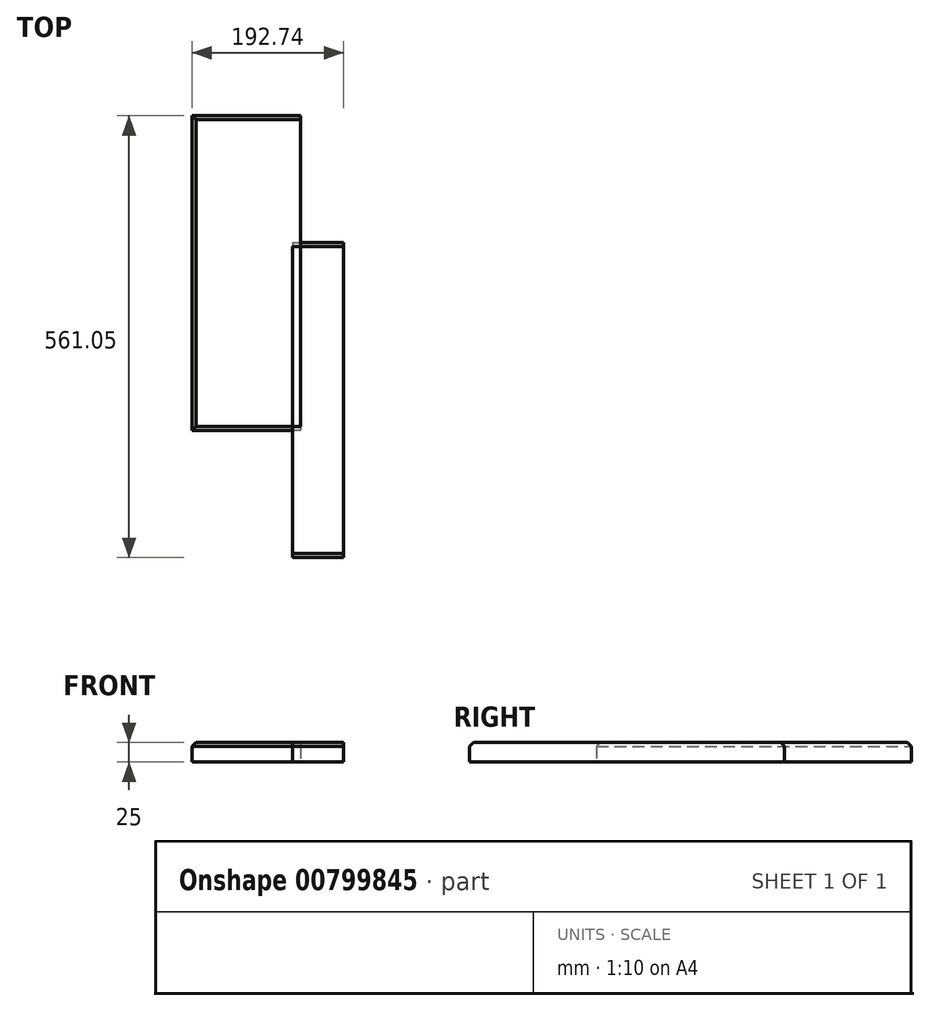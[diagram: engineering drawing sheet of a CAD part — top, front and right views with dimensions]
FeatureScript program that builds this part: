
annotation { "Feature Type Name" : "Feature", "Feature Type Description" : "" }
export const myFeature = defineFeature(function(context is Context, id is Id, definition is map)
    precondition{}
    {
        {
            var Q0;
            Q0=qCreatedBy(makeId("Top.planeOp"),FACE);
            var sketch = newSketch(context, id + "F0", { "sketchPlane" : qUnion([Q0])});
            skLineSegment(sketch, "E0", {"start": v(-106.87, 169.05) * mm, "end": v(106.6, -169.22) * mm});
            skLineSegment(sketch, "E1", {"start": v(106.6, -169.22) * mm, "end": v(-106.87, 169.05) * mm});
            skArc(sketch, "E2", {"start": v(106.6, -169.22) * mm, "mid": v(169.14, 106.74) * mm, "end": v(-106.87, 169.05) * mm});
            skSolve(sketch);
        }
        {
            var Q0;
            Q0=qCreatedBy(makeId("Top.planeOp"),FACE);
            var sketch = newSketch(context, id + "F1", { "sketchPlane" : qUnion([Q0])});
            skLineSegment(sketch, "E3.bottom", {"start": v(-271.16, 238.95) * mm, "end": v(-206.16, 238.95) * mm});
            skLineSegment(sketch, "E3.top", {"start": v(-271.16, -161.05) * mm, "end": v(-206.16, -161.05) * mm});
            skLineSegment(sketch, "E3.left", {"start": v(-271.16, 238.95) * mm, "end": v(-271.16, -161.05) * mm});
            skLineSegment(sketch, "E3.right", {"start": v(-206.16, 238.95) * mm, "end": v(-206.16, -161.05) * mm});
            skSolve(sketch);
        }
        {
            var Q0;
            Q0=qCreatedBy(makeId("Top.planeOp"),FACE);
            var sketch = newSketch(context, id + "F2", { "sketchPlane" : qUnion([Q0])});
            skLineSegment(sketch, "E4.bottom", {"start": v(-398.9, 400) * mm, "end": v(-260.9, 400) * mm});
            skLineSegment(sketch, "E4.top", {"start": v(-398.9, 0) * mm, "end": v(-260.9, 0) * mm});
            skLineSegment(sketch, "E4.left", {"start": v(-398.9, 400) * mm, "end": v(-398.9, 0) * mm});
            skLineSegment(sketch, "E4.right", {"start": v(-260.9, 400) * mm, "end": v(-260.9, 0) * mm});
            skSolve(sketch);
        }
        {
            var Q0;
            Q0=makeQuery(id+"F2.imprint","IMPRINT",FACE,{"disambiguationData":[TD([[makeQuery(id+"F2.imprint","IMPRINT",EDGE,{"derivedFrom":sQuery(id+"F2.wireOp",EDGE,"E4.bottom")}),-1.0]])]});
            var Q1;
            Q1=makeQuery(id+"F1.imprint","IMPRINT",FACE,{"disambiguationData":[TD([[makeQuery(id+"F1.imprint","IMPRINT",EDGE,{"derivedFrom":sQuery(id+"F1.wireOp",EDGE,"E3.bottom")}),-1.0]])]});
            var Q2;
            Q2=makeQuery(id+"F0.imprint","IMPRINT",FACE,{"disambiguationData":[TD([[makeQuery(id+"F0.imprint","IMPRINT",EDGE,{"derivedFrom":sQuery(id+"F0.wireOp",EDGE,"E1")}),-1.0]])]});
            extrude(context, id + "F3", {"entities" : qUnion([Q0, Q1, Q2]), "depth" : 25 * mm, "offsetDistance" : 25 * mm});
        }
        {
            var Q0;
            Q0=makeQuery(id+"F3.opExtrude","CAP_EDGE",EDGE,{"disambiguationData":[OSD([sQuery(id+"F2.wireOp",EDGE,"E4.top")])],"isStart":false});
            var Q1;
            Q1=makeQuery(id+"F3.opExtrude","CAP_EDGE",EDGE,{"disambiguationData":[OSD([sQuery(id+"F1.wireOp",EDGE,"E3.top")])],"isStart":false});
            var Q2;
            Q2=makeQuery(id+"F3.opExtrude","CAP_EDGE",EDGE,{"disambiguationData":[OSD([sQuery(id+"F0.wireOp",EDGE,"E2")])],"isStart":false});
            var Q3;
            Q3=makeQuery(id+"F3.opExtrude","CAP_EDGE",EDGE,{"disambiguationData":[OSD([sQuery(id+"F1.wireOp",EDGE,"E3.bottom")])],"isStart":false});
            var Q4;
            Q4=makeQuery(id+"F3.opExtrude","CAP_EDGE",EDGE,{"disambiguationData":[OSD([sQuery(id+"F2.wireOp",EDGE,"E4.bottom")])],"isStart":false});
            var Q5;
            Q5=makeQuery(id+"F3.opExtrude","CAP_EDGE",EDGE,{"disambiguationData":[OSD([sQuery(id+"F2.wireOp",EDGE,"E4.left")])],"isStart":false});
            chamfer(context, id + "F4", {"entities" : qUnion([Q0, Q1, Q2, Q3, Q4, Q5]), "width" : 5 * mm, "tangentPropagation" : true});
        }
    });
